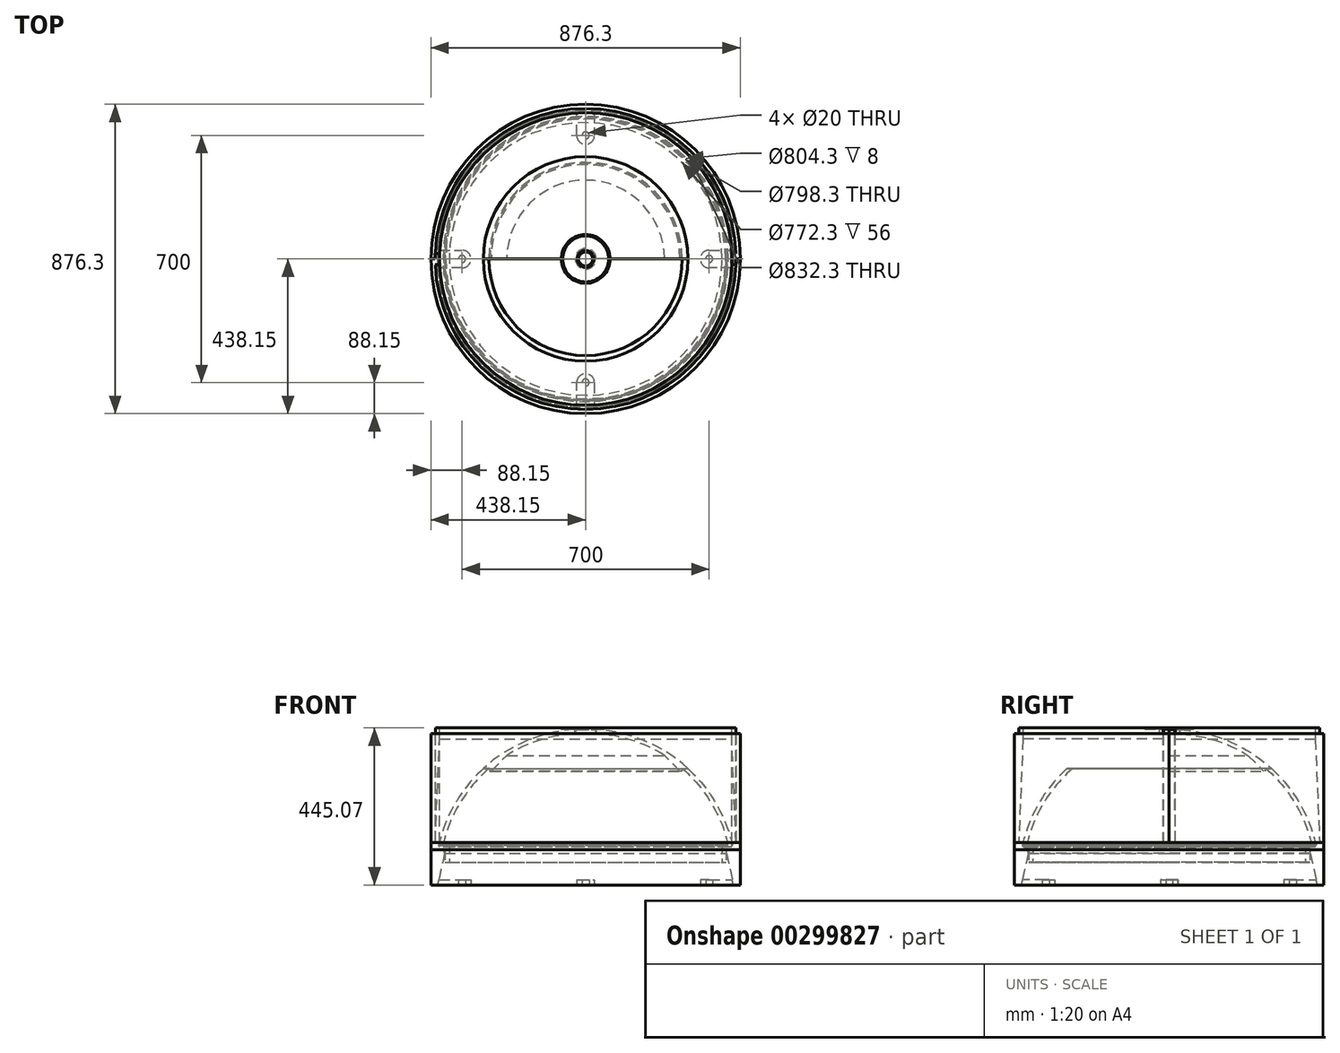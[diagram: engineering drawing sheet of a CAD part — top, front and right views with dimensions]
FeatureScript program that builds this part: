
annotation { "Feature Type Name" : "Feature", "Feature Type Description" : "" }
export const myFeature = defineFeature(function(context is Context, id is Id, definition is map)
    precondition{}
    {
        {
            var Q0;
            Q0=qCreatedBy(makeId("Front.planeOp"),FACE);
            var sketch = newSketch(context, id + "F0", { "sketchPlane" : qUnion([Q0])});
            skLineSegment(sketch, "E0", {"start": v(0, 0) * mm, "end": v(0, 98.6) * mm});
            skSolve(sketch);
        }
        {
            var Q0;
            Q0=qCreatedBy(makeId("Top.planeOp"),FACE);
            var sketch = newSketch(context, id + "F1", { "sketchPlane" : qUnion([Q0])});
            skArc(sketch, "E1", {"start": v(438.15, 0) * mm, "mid": v(0, 438.15) * mm, "end": v(-438.15, 0) * mm});
            skLineSegment(sketch, "E2", {"start": v(426.15, 0) * mm, "end": v(438.15, 0) * mm});
            skLineSegment(sketch, "E3", {"start": v(-426.15, 0) * mm, "end": v(-438.15, 0) * mm});
            skArc(sketch, "E4", {"start": v(426.15, 0) * mm, "mid": v(0, 426.15) * mm, "end": v(-426.15, 0) * mm});
            skSolve(sketch);
        }
        {
            var Q0;
            Q0 = qSketchRegion(id + "F1", true);
            extrude(context, id + "F2", {"entities" : qUnion([Q0]), "depth" : 309 * mm});
        }
        {
            var Q0;
            Q0=qCreatedBy(makeId("Top.planeOp"),FACE);
            var sketch = newSketch(context, id + "F3", { "sketchPlane" : qUnion([Q0])});
            skLineSegment(sketch, "E5", {"start": v(0, 0) * mm, "end": v(420.15, 0) * mm});
            skLineSegment(sketch, "E6.bottom", {"start": v(426.15, 16) * mm, "end": v(414.15, 16) * mm});
            skLineSegment(sketch, "E6.top", {"start": v(426.15, -16) * mm, "end": v(414.15, -16) * mm});
            skLineSegment(sketch, "E6.left", {"start": v(426.15, 16) * mm, "end": v(426.15, -16) * mm});
            skLineSegment(sketch, "E6.right", {"start": v(414.15, 16) * mm, "end": v(414.15, -16) * mm});
            skPoint(sketch, "E6.middle", {"position": v(420.15, 0) * mm});
            skSolve(sketch);
        }
        {
            var Q0;
            Q0 = qSketchRegion(id + "F3", true);
            var Q1;
            Q1=makeQuery(id+"F2.opExtrude","SWEPT_EDGE",EDGE,{"disambiguationData":[OSD([sQuery(id+"F1.wireOp",EDGE,"E2"),sQuery(id+"F1.wireOp",EDGE,"E4")])]});
            sweep(context, id + "F4", {"operationType" : NewBodyOperationType.ADD, "profiles" : qUnion([Q0]), "path" : qUnion([Q1])});
        }
        {
            var Q0;
            Q0=qCreatedBy(makeId("Front.planeOp"),FACE);
            var sketch = newSketch(context, id + "F5", { "sketchPlane" : qUnion([Q0])});
            skLineSegment(sketch, "E7", {"start": v(0, 0) * mm, "end": v(0, 309) * mm});
            skLineSegment(sketch, "E8", {"start": v(0, 309) * mm, "end": v(-420.15, 309) * mm});
            skLineSegment(sketch, "E9.bottom", {"start": v(-426.15, 293) * mm, "end": v(-414.15, 293) * mm});
            skLineSegment(sketch, "E9.top", {"start": v(-426.15, 325) * mm, "end": v(-414.15, 325) * mm});
            skLineSegment(sketch, "E9.left", {"start": v(-426.15, 293) * mm, "end": v(-426.15, 325) * mm});
            skLineSegment(sketch, "E9.right", {"start": v(-414.15, 293) * mm, "end": v(-414.15, 325) * mm});
            skPoint(sketch, "E9.middle", {"position": v(-420.15, 309) * mm});
            skLineSegment(sketch, "E10", {"start": v(-426.15, 293) * mm, "end": v(-426.15, 0) * mm});
            skLineSegment(sketch, "E11", {"start": v(-426.15, 0) * mm, "end": v(-414.15, 293) * mm});
            skSolve(sketch);
        }
        {
            var Q0;
            Q0 = qSketchRegion(id + "F5", true);
            var Q1;
            Q1=sQuery(id+"F5.wireOp",EDGE,"E7");
            revolve(context, id + "F6", {"operationType" : NewBodyOperationType.ADD, "entities" : qUnion([Q0]), "axis" : qUnion([Q1]), "revolveType" : RevolveType.TWO_DIRECTIONS, "angle" : 357.75 * degree, "angleBack" : 182.25 * degree});
        }
        {
            var Q0;
            Q0=qCreatedBy(makeId("Front.planeOp"),FACE);
            var sketch = newSketch(context, id + "F7", { "sketchPlane" : qUnion([Q0])});
            skLineSegment(sketch, "E12.left", {"start": v(0, 0) * mm, "end": v(0, -50) * mm});
            skLineSegment(sketch, "E12.right", {"start": v(438.15, 0) * mm, "end": v(438.15, -20) * mm});
            skLineSegment(sketch, "E13", {"start": v(0, 0) * mm, "end": v(0, 304) * mm});
            skLineSegment(sketch, "E14", {"start": v(398.15, -20) * mm, "end": v(438.15, -20) * mm});
            skLineSegment(sketch, "E15.top", {"start": v(398.15, -56) * mm, "end": v(386.15, -56) * mm});
            skLineSegment(sketch, "E15.right", {"start": v(386.15, 0) * mm, "end": v(386.15, -56) * mm});
            skLineSegment(sketch, "E16", {"start": v(398.15, -56) * mm, "end": v(398.15, -20) * mm});
            skLineSegment(sketch, "E17", {"start": v(416.15, 0) * mm, "end": v(416.15, -12) * mm});
            skLineSegment(sketch, "E18", {"start": v(416.15, -12) * mm, "end": v(400.15, -12) * mm});
            skLineSegment(sketch, "E19", {"start": v(400.15, -12) * mm, "end": v(400.15, 0) * mm});
            skLineSegment(sketch, "E20", {"start": v(386.15, 0) * mm, "end": v(400.15, 0) * mm});
            skLineSegment(sketch, "E21", {"start": v(416.15, 0) * mm, "end": v(438.15, 0) * mm});
            skSolve(sketch);
        }
        {
            var Q0;
            Q0 = qSketchRegion(id + "F7", true);
            var Q1;
            Q1=sQuery(id+"F0.wireOp",EDGE,"E0");
            revolve(context, id + "F8", {"entities" : qUnion([Q0]), "axis" : qUnion([Q1]), "revolveType" : RevolveType.FULL});
        }
        {
            var Q0;
            Q0=makeQuery(id+"F8.opRevolve","SWEPT_EDGE",EDGE,{"disambiguationData":[OSD([sQuery(id+"F7.wireOp",EDGE,"E17"),sQuery(id+"F7.wireOp",EDGE,"E21")])]});
            var Q1;
            Q1=makeQuery(id+"F8.opRevolve","SWEPT_EDGE",EDGE,{"disambiguationData":[OSD([sQuery(id+"F7.wireOp",EDGE,"E19"),sQuery(id+"F7.wireOp",EDGE,"E20")])]});
            var Q2;
            Q2=makeQuery(id+"F8.opRevolve","SWEPT_FACE",FACE,{"disambiguationData":[OSD([sQuery(id+"F7.wireOp",EDGE,"E18")])]});
            chamfer(context, id + "F9", {"entities" : qUnion([Q0, Q1, Q2]), "width" : 4 * mm, "tangentPropagation" : true});
        }
        {
            var Q0;
            Q0=qCreatedBy(makeId("Front.planeOp"),FACE);
            var sketch = newSketch(context, id + "F10", { "sketchPlane" : qUnion([Q0])});
            skLineSegment(sketch, "E22.left", {"start": v(0, 0) * mm, "end": v(0, -50) * mm});
            skLineSegment(sketch, "E23", {"start": v(0, 0) * mm, "end": v(0, 308) * mm});
            skArc(sketch, "E24", {"start": v(414.15, 0) * mm, "mid": v(367.5, 114.25) * mm, "end": v(289.64, 210) * mm});
            skArc(sketch, "E25", {"start": v(402.15, 0) * mm, "mid": v(354.27, 115.03) * mm, "end": v(273.6, 210) * mm});
            skLineSegment(sketch, "E26", {"start": v(0, 308) * mm, "end": v(0, 320) * mm});
            skLineSegment(sketch, "E27.bottom", {"start": v(402.15, 0) * mm, "end": v(414.15, 0) * mm});
            skLineSegment(sketch, "E27.top", {"start": v(402.15, -8) * mm, "end": v(414.15, -8) * mm});
            skLineSegment(sketch, "E27.left", {"start": v(402.15, 0) * mm, "end": v(402.15, -8) * mm});
            skLineSegment(sketch, "E27.right", {"start": v(414.15, 0) * mm, "end": v(414.15, -8) * mm});
            skLineSegment(sketch, "E28", {"start": v(273.6, 210) * mm, "end": v(289.64, 210) * mm});
            skSolve(sketch);
        }
        {
            var Q0;
            Q0 = qSketchRegion(id + "F10", true);
            var Q1;
            Q1=sQuery(id+"F10.wireOp",EDGE,"E23");
            revolve(context, id + "F11", {"entities" : qUnion([Q0]), "axis" : qUnion([Q1]), "revolveType" : RevolveType.ONE_DIRECTION, "angle" : 360 * degree});
        }
        {
            var Q0;
            Q0=qCreatedBy(makeId("Front.planeOp"),FACE);
            var sketch = newSketch(context, id + "F12", { "sketchPlane" : qUnion([Q0])});
            skLineSegment(sketch, "E29.left", {"start": v(0, 0) * mm, "end": v(0, -50) * mm});
            skLineSegment(sketch, "E30", {"start": v(0, 0) * mm, "end": v(0, 308.43) * mm});
            skArc(sketch, "E31", {"start": v(289.63, 210) * mm, "mid": v(169.32, 287.44) * mm, "end": v(30, 320) * mm});
            skArc(sketch, "E32", {"start": v(273.56, 210) * mm, "mid": v(159.96, 279.34) * mm, "end": v(30, 308) * mm});
            skLineSegment(sketch, "E33", {"start": v(30, 308) * mm, "end": v(30, 320) * mm});
            skLineSegment(sketch, "E34", {"start": v(273.56, 210) * mm, "end": v(289.63, 210) * mm});
            skLineSegment(sketch, "E35", {"start": v(273.56, 210) * mm, "end": v(271.56, 210) * mm});
            skLineSegment(sketch, "E36", {"start": v(271.56, 210) * mm, "end": v(271.56, 202) * mm});
            skLineSegment(sketch, "E37", {"start": v(271.56, 202) * mm, "end": v(267.56, 202) * mm});
            skLineSegment(sketch, "E38", {"start": v(267.56, 202) * mm, "end": v(267.56, 215.1) * mm});
            skSolve(sketch);
        }
        {
            var Q0;
            Q0 = qSketchRegion(id + "F12", true);
            var Q1;
            Q1=sQuery(id+"F12.wireOp",EDGE,"E30");
            revolve(context, id + "F13", {"entities" : qUnion([Q0]), "axis" : qUnion([Q1]), "revolveType" : RevolveType.ONE_DIRECTION, "angle" : 180 * degree});
        }
        {
            var Q0;
            Q0=makeQuery(id+"F13.opRevolve","SWEPT_EDGE",EDGE,{"disambiguationData":[OSD([sQuery(id+"F12.wireOp",EDGE,"E32"),sQuery(id+"F12.wireOp",EDGE,"E38")])]});
            chamfer(context, id + "F14", {"entities" : qUnion([Q0]), "chamferType" : ChamferType.TWO_OFFSETS, "width1" : 50 * mm, "oppositeDirection" : false, "width2" : 9 * mm, "tangentPropagation" : true});
        }
        {
            var Q0;
            Q0=makeQuery(id+"F8.opRevolve","SWEPT_FACE",FACE,{"disambiguationData":[OSD([sQuery(id+"F7.wireOp",EDGE,"E14")])]});
            var sketch = newSketch(context, id + "F15", { "sketchPlane" : qUnion([Q0])});
            skCircle(sketch, "E39", {"center": v(0, 0) * mm, "radius": 399.15 * mm});
            skCircle(sketch, "E40", {"center": v(0, 0) * mm, "radius": 438.15 * mm});
            skSolve(sketch);
        }
        {
            var Q0;
            Q0 = qSketchRegion(id + "F15", true);
            extrude(context, id + "F16", {"entities" : qUnion([Q0]), "depth" : 100 * mm, "offsetDistance" : 25 * mm});
        }
        {
            var Q0;
            Q0=makeQuery(id+"F16.opExtrude","CAP_EDGE",EDGE,{"disambiguationData":[OSD([sQuery(id+"F15.wireOp",EDGE,"E39")])],"isStart":true});
            chamfer(context, id + "F17", {"entities" : qUnion([Q0]), "width" : 2 * mm, "tangentPropagation" : true});
        }
        {
            var Q0;
            Q0=makeQuery(id+"F2.opExtrude","SWEPT_BODY",BODY,{"disambiguationData":[OSD([sQuery(id+"F1.wireOp",EDGE,"E1"),sQuery(id+"F1.wireOp",EDGE,"E2"),sQuery(id+"F1.wireOp",EDGE,"E3"),sQuery(id+"F1.wireOp",EDGE,"E4")])]});
            var Q1;
            Q1=sQuery(id+"F0.wireOp",EDGE,"E0");
            transform(context, id + "F18", {"entities" : qUnion([Q0]), "transformType" : TransformType.ROTATION, "transformAxis" : qUnion([Q1]), "angle" : 180 * degree, "makeCopy" : true});
        }
        {
            var Q0;
            Q0=makeQuery(id+"F16.opExtrude","CAP_EDGE",EDGE,{"disambiguationData":[OSD([sQuery(id+"F15.wireOp",EDGE,"E39")])],"isStart":false});
            chamfer(context, id + "F19", {"entities" : qUnion([Q0]), "chamferType" : ChamferType.TWO_OFFSETS, "width1" : 90 * mm, "oppositeDirection" : false, "width2" : 20 * mm, "tangentPropagation" : true});
        }
        {
            var Q0;
            Q0=makeQuery(id+"F16.opExtrude","CAP_FACE",FACE,{"disambiguationData":[OSD([sQuery(id+"F15.wireOp",EDGE,"E39"),sQuery(id+"F15.wireOp",EDGE,"E40")])],"isStart":false});
            var sketch = newSketch(context, id + "F20", { "sketchPlane" : qUnion([Q0])});
            skArc(sketch, "E41", {"start": v(350, 25) * mm, "mid": v(325, 0) * mm, "end": v(350, -25) * mm});
            skCircle(sketch, "E42", {"center": v(350, 0) * mm, "radius": 10 * mm});
            skLineSegment(sketch, "E43", {"start": v(350, -25) * mm, "end": v(428.15, -25) * mm});
            skLineSegment(sketch, "E44", {"start": v(428.15, -25) * mm, "end": v(428.15, 25) * mm});
            skLineSegment(sketch, "E45", {"start": v(428.15, 25) * mm, "end": v(350, 25) * mm});
            skLineSegment(sketch, "E46.1.0", {"start": v(25, 350) * mm, "end": v(25, 428.15) * mm});
            skLineSegment(sketch, "E46.1.1", {"start": v(-25, 428.15) * mm, "end": v(-25, 350) * mm});
            skArc(sketch, "E46.1.2", {"start": v(-25, 350) * mm, "mid": v(0, 325) * mm, "end": v(25, 350) * mm});
            skLineSegment(sketch, "E46.1.3", {"start": v(25, 428.15) * mm, "end": v(-25, 428.15) * mm});
            skCircle(sketch, "E46.1.4", {"center": v(0, 350) * mm, "radius": 10 * mm});
            skLineSegment(sketch, "E46.2.0", {"start": v(-350, 25) * mm, "end": v(-428.15, 25) * mm});
            skLineSegment(sketch, "E46.2.1", {"start": v(-428.15, -25) * mm, "end": v(-350, -25) * mm});
            skArc(sketch, "E46.2.2", {"start": v(-350, -25) * mm, "mid": v(-325, 0) * mm, "end": v(-350, 25) * mm});
            skLineSegment(sketch, "E46.2.3", {"start": v(-428.15, 25) * mm, "end": v(-428.15, -25) * mm});
            skCircle(sketch, "E46.2.4", {"center": v(-350, 0) * mm, "radius": 10 * mm});
            skLineSegment(sketch, "E46.3.0", {"start": v(-25, -350) * mm, "end": v(-25, -428.15) * mm});
            skLineSegment(sketch, "E46.3.1", {"start": v(25, -428.15) * mm, "end": v(25, -350) * mm});
            skArc(sketch, "E46.3.2", {"start": v(25, -350) * mm, "mid": v(0, -325) * mm, "end": v(-25, -350) * mm});
            skLineSegment(sketch, "E46.3.3", {"start": v(-25, -428.15) * mm, "end": v(25, -428.15) * mm});
            skCircle(sketch, "E46.3.4", {"center": v(0, -350) * mm, "radius": 10 * mm});
            skPoint(sketch, "E46.center", {"position": v(0, 0) * mm});
            skSolve(sketch);
        }
        {
            var Q0;
            Q0 = qSketchRegion(id + "F20", true);
            extrude(context, id + "F21", {"entities" : qUnion([Q0]), "operationType" : NewBodyOperationType.ADD, "oppositeDirection" : true, "depth" : 15 * mm, "offsetDistance" : 25 * mm});
        }
        {
            var Q0;
            Q0=makeQuery(id+"F13.opRevolve","CAP_FACE",FACE,{"disambiguationData":[OSD([sQuery(id+"F12.wireOp",EDGE,"E31"),sQuery(id+"F12.wireOp",EDGE,"E32"),sQuery(id+"F12.wireOp",EDGE,"E33"),sQuery(id+"F12.wireOp",EDGE,"E34"),sQuery(id+"F12.wireOp",EDGE,"E35"),sQuery(id+"F12.wireOp",EDGE,"E36"),sQuery(id+"F12.wireOp",EDGE,"E37"),sQuery(id+"F12.wireOp",EDGE,"E38")])],"isStart":true});
            var sketch = newSketch(context, id + "F22", { "sketchPlane" : qUnion([Q0])});
            skLineSegment(sketch, "E47", {"start": v(0, 307.07) * mm, "end": v(0, 325.07) * mm});
            skLineSegment(sketch, "E48", {"start": v(0, 325.07) * mm, "end": v(20, 325.07) * mm});
            skLineSegment(sketch, "E49", {"start": v(65, 325.07) * mm, "end": v(69, 321.07) * mm});
            skLineSegment(sketch, "E50", {"start": v(0, 307.07) * mm, "end": v(29, 307.07) * mm});
            skLineSegment(sketch, "E51", {"start": v(29, 307.07) * mm, "end": v(29, 321.07) * mm});
            skLineSegment(sketch, "E52", {"start": v(29, 321.07) * mm, "end": v(69, 321.07) * mm});
            skLineSegment(sketch, "E53", {"start": v(20, 325.07) * mm, "end": v(20, 322.07) * mm});
            skLineSegment(sketch, "E54", {"start": v(20, 322.07) * mm, "end": v(22, 320.07) * mm});
            skLineSegment(sketch, "E55", {"start": v(22, 320.07) * mm, "end": v(22, 322.39) * mm});
            skLineSegment(sketch, "E56.MirrorCS", {"start": v(24, 322.07) * mm, "end": v(22, 320.07) * mm});
            skLineSegment(sketch, "E57.MirrorCS", {"start": v(24, 325.07) * mm, "end": v(24, 322.07) * mm});
            skLineSegment(sketch, "E58.trimOffspring", {"start": v(24, 325.07) * mm, "end": v(65, 325.07) * mm});
            skSolve(sketch);
        }
        {
            var Q0;
            Q0 = qSketchRegion(id + "F22", true);
            var Q1;
            Q1=sQuery(id+"F22.wireOp",EDGE,"E47");
            revolve(context, id + "F23", {"surfaceOperationType" : NewSurfaceOperationType.NEW, "entities" : qUnion([Q0]), "axis" : qUnion([Q1]), "revolveType" : RevolveType.FULL});
        }
        {
            var Q0;
            Q0=makeQuery(id+"F23.opRevolve","SWEPT_FACE",FACE,{"disambiguationData":[OSD([sQuery(id+"F22.wireOp",EDGE,"E48")])]});
            var Q1;
            Q1=makeQuery(id+"F23.opRevolve","SWEPT_EDGE",EDGE,{"disambiguationData":[OSD([sQuery(id+"F22.wireOp",EDGE,"E57.MirrorCS"),sQuery(id+"F22.wireOp",EDGE,"E58.trimOffspring")])]});
            fillet(context, id + "F24", {"entities" : qUnion([Q0, Q1]), "tangentPropagation" : true, "radius" : 3 * mm, "defaultsChanged" : false, "vertexSettings" : [], "allowEdgeOverflow" : false});
        }
    });
